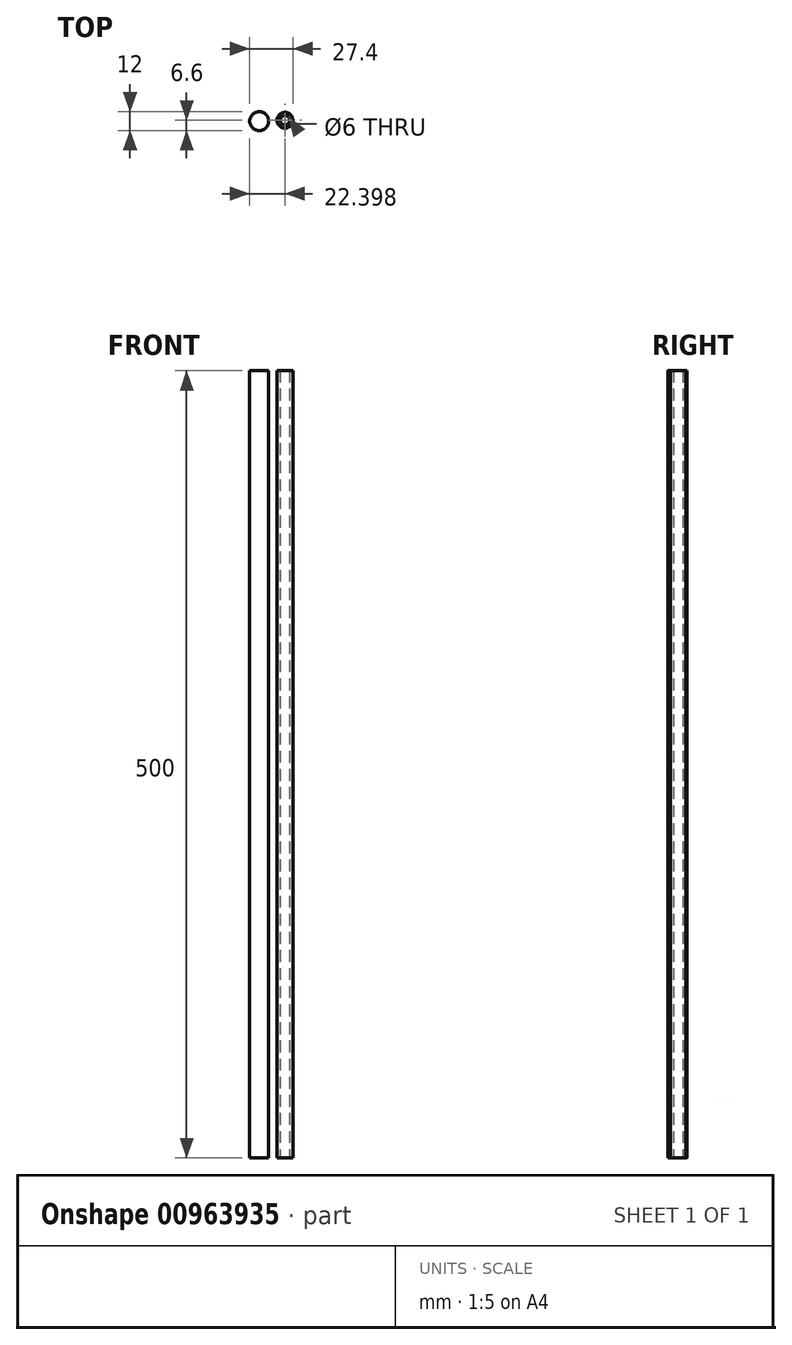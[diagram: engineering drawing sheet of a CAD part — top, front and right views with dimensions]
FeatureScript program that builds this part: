
annotation { "Feature Type Name" : "Feature", "Feature Type Description" : "" }
export const myFeature = defineFeature(function(context is Context, id is Id, definition is map)
    precondition{}
    {
        {
            var Q0;
            Q0=qCreatedBy(makeId("Top.planeOp"),FACE);
            var sketch = newSketch(context, id + "F0", { "sketchPlane" : qUnion([Q0])});
            skCircle(sketch, "E0", {"center": v(-39.16, 52.8) * mm, "radius": 6 * mm});
            skCircle(sketch, "E1", {"center": v(-22.76, 53.4) * mm, "radius": 5 * mm});
            skCircle(sketch, "E2.0", {"center": v(-22.76, 53.4) * mm, "radius": 3 * mm});
            skSolve(sketch);
        }
        {
            var Q0;
            Q0=makeQuery(id+"F0.imprint","IMPRINT",FACE,{"disambiguationData":[TD([[makeQuery(id+"F0.imprint","IMPRINT",EDGE,{"derivedFrom":sQuery(id+"F0.wireOp",EDGE,"E0")}),1.0]])]});
            var Q1;
            Q1=makeQuery(id+"F0.imprint","IMPRINT",FACE,{"disambiguationData":[TD([[makeQuery(id+"F0.imprint","IMPRINT",EDGE,{"derivedFrom":sQuery(id+"F0.wireOp",EDGE,"E1")}),1.0]])]});
            extrude(context, id + "F1", {"entities" : qUnion([Q0, Q1]), "depth" : 500 * mm, "offsetDistance" : 25 * mm});
        }
    });
